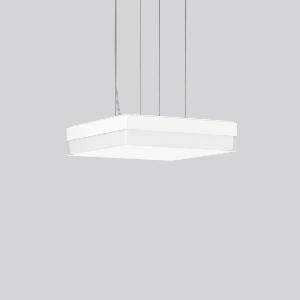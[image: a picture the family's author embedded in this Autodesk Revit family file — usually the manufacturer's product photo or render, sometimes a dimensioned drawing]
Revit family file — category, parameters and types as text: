
# Revit family: flat_slim_square_312542_002_76_79b6
name_source: partatom
category: Lighting Fixtures
units: mm (PartAtom-declared; Revit-internal decimal feet)

## family parameters
Cut with Voids When Loaded = No
Host = Face
Light Source = No
Part Type = Normal
Room Calculation Point = No
Round Connector Dimension = Use Diameter
Shared = No

## types (1)
- MultiLumen 2 840 (1 x LED Modul 840, 2300 lm, 4000)
    Apparent Load = 21 VA
    CIE Flux Codes = 43 75 93 91 100
    Color Rendering = 80
    Color Temperature = 4000
    Default Elevation = 1800 mm
    Height = 70 mm
    Lamp = 1 x LED Modul 840
    Lamp Light Flux = 2300 lm
    Lamp count = 1
    Length = 300 mm
    Lifetime = 50000 h
    Luminous efficacy = 110 lm/W
    Manufacturer = RZB
    ModVariant = No
    Model = 312542.002.76
    Mounting Place = Ceiling
    Mounting Type = Pendant
    Number of Poles = 1
    OnlyDefault = Yes
    Power Factor = 1
    Product Name = FLAT SLIM square
    Product group = Pendant luminaires
    ProductGroupID = 902
    Protection Class = Protection class I
    Protection Degree = IP 40
    RLX_Detail_Level = 1
    RLX_Emergency_Light_Flux = 0 lm
    RLX_Emergency_Type = 0
    RLX_Emergency_Type_DB = No
    RlxData = <blob elided: 13669 chars, md5=4734781c>
    Socket = socket
    Standby Power = 0 W
    System Light Flux = 2300 lm
    System Power = 21 W
    Type Comments = MultiLumen 2 840
    Type Image = 312542.002.jpg
    URL = http://relux.com
    VarID = multilumen_2_840
    Voltage = 230 V
    Voltage Range = 220-240 V
    Weight = 0.00 kg
    Width = 300 mm

## geometry (parser evidence)
native form markers: Sweep x12
no freeform markers — native parametric forms only
